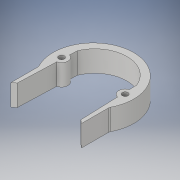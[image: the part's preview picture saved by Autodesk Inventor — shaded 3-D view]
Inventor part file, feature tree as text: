
AUTODESK INVENTOR PART (.ipt)
format: ipt  version: 2019.2 (Build 232265000, 265)  size: 142,848 bytes
history: native  units: mm
features: sketch x2, other x1, extrude x1
ambient origin geometry x8: Origin, YZ Plane, XZ Plane, XY Plane, X Axis, Y Axis, Z Axis, Center Point
bodies: Solid1 (feature_tree)
feature tree (4):
  other  "Motor Holder.ipt"
  extrude  "Extrusion1"  Depth=40.0mm
  sketch  "Sketch8"  dims[d5=2.5mm d6=2.5mm d8=15.0mm d9=0.0mm]
  sketch  "Sketch2"  dims[d0=10.0mm d1=40.0mm]
